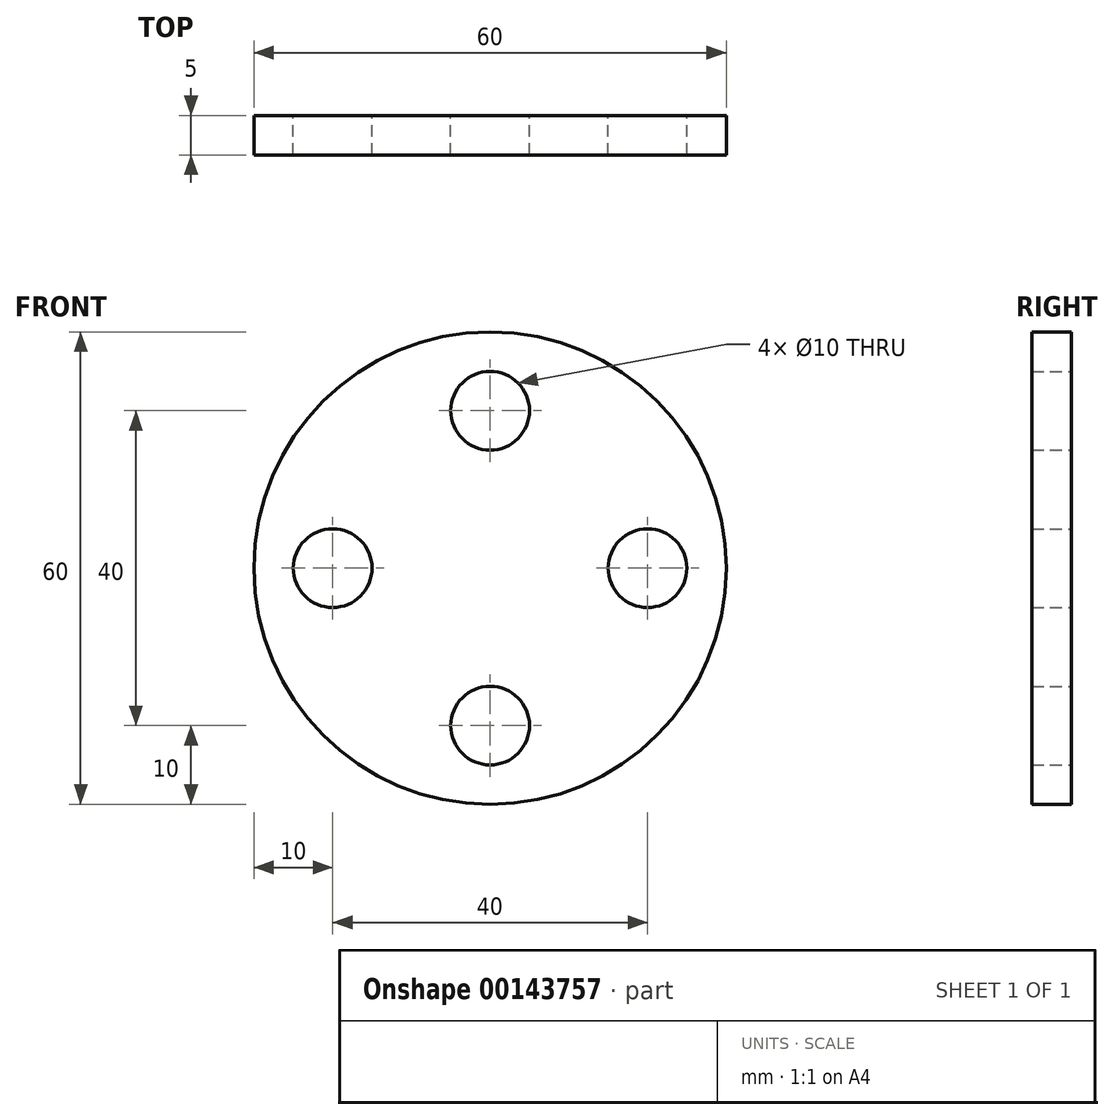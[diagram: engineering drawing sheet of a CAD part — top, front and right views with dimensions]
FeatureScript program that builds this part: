
annotation { "Feature Type Name" : "Feature", "Feature Type Description" : "" }
export const myFeature = defineFeature(function(context is Context, id is Id, definition is map)
    precondition{}
    {
        {
            var Q0;
            Q0=qCreatedBy(makeId("Front.planeOp"),FACE);
            var sketch = newSketch(context, id + "F0", { "sketchPlane" : qUnion([Q0])});
            skCircle(sketch, "E0", {"center": v(0, 0) * mm, "radius": 20 * mm, "construction": true});
            skCircle(sketch, "E1", {"center": v(0, 0) * mm, "radius": 30 * mm});
            skLineSegment(sketch, "E2", {"start": v(0, 51.25) * mm, "end": v(0, -48.67) * mm, "construction": true});
            skLineSegment(sketch, "E3", {"start": v(-50.53, 0) * mm, "end": v(59.72, 0) * mm, "construction": true});
            skCircle(sketch, "E4", {"center": v(0, -20) * mm, "radius": 5 * mm});
            skCircle(sketch, "E5", {"center": v(20, 0) * mm, "radius": 5 * mm});
            skCircle(sketch, "E6", {"center": v(-20, 0) * mm, "radius": 5 * mm});
            skCircle(sketch, "E7", {"center": v(0, 20) * mm, "radius": 5 * mm});
            skSolve(sketch);
        }
        {
            var Q0;
            Q0=qSketchRegion(id+"F0",true);
            extrude(context, id + "F1", {"entities" : qUnion([Q0]), "depth" : 5 * mm});
        }
    });
